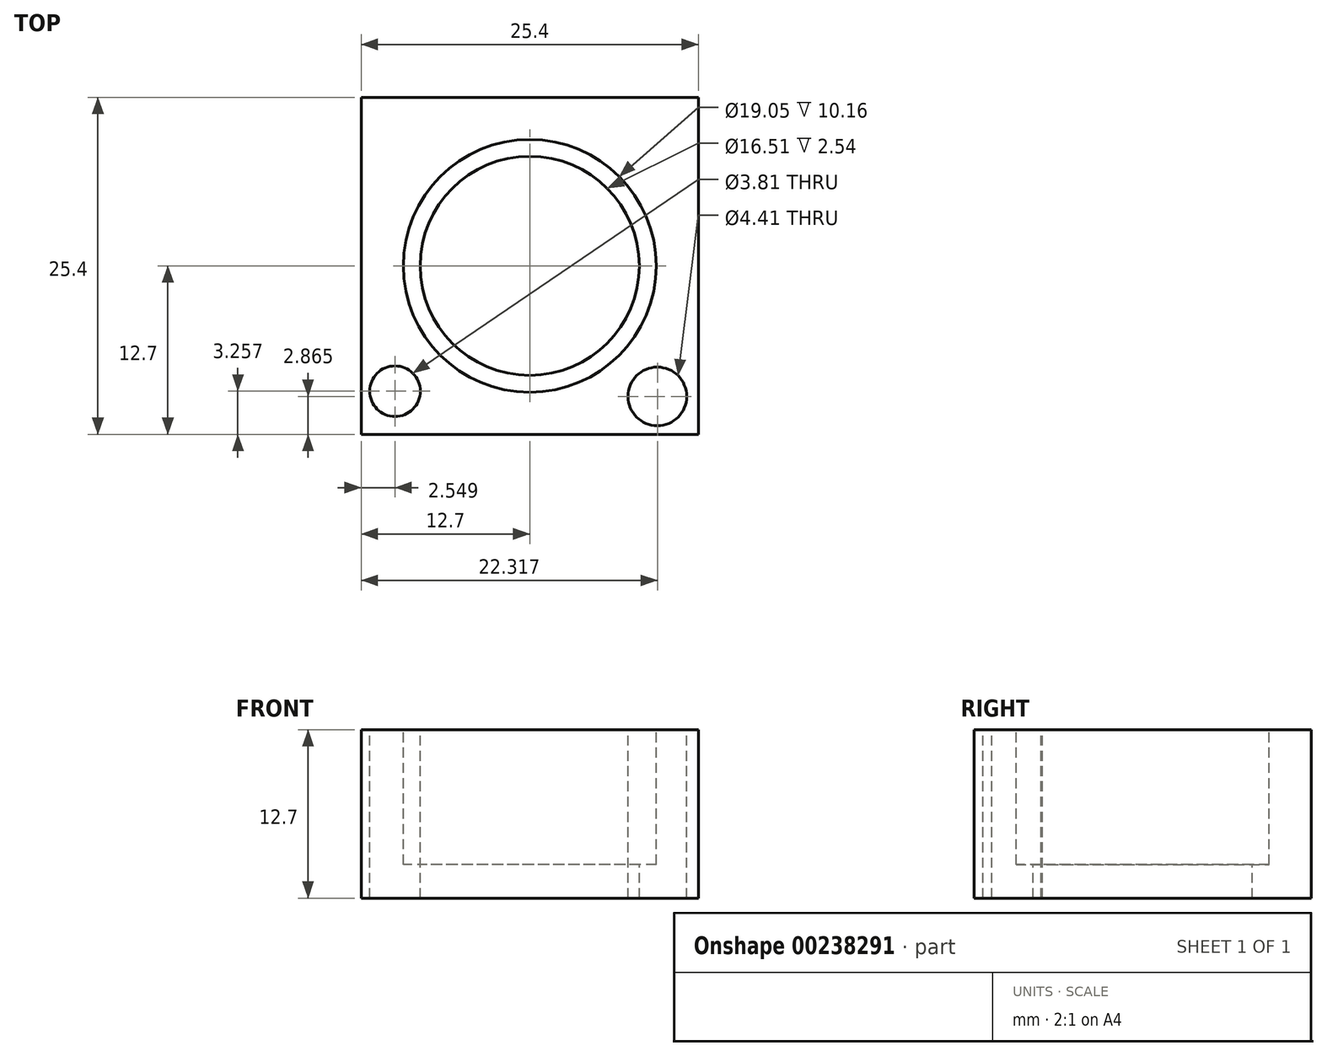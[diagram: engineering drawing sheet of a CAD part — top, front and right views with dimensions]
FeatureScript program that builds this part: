
annotation { "Feature Type Name" : "Feature", "Feature Type Description" : "" }
export const myFeature = defineFeature(function(context is Context, id is Id, definition is map)
    precondition{}
    {
        {
            var Q0;
            Q0=qCreatedBy(makeId("Top.planeOp"),FACE);
            var sketch = newSketch(context, id + "F0", { "sketchPlane" : qUnion([Q0])});
            skLineSegment(sketch, "E0.bottom", {"start": v(0, 0) * mm, "end": v(25.4, 0) * mm});
            skLineSegment(sketch, "E0.top", {"start": v(0, 25.4) * mm, "end": v(25.4, 25.4) * mm});
            skLineSegment(sketch, "E0.left", {"start": v(0, 0) * mm, "end": v(0, 25.4) * mm});
            skLineSegment(sketch, "E0.right", {"start": v(25.4, 0) * mm, "end": v(25.4, 25.4) * mm});
            skSolve(sketch);
        }
        {
            var Q0;
            Q0 = qSketchRegion(id + "F0", true);
            extrude(context, id + "F1", {"entities" : qUnion([Q0]), "depth" : 12.7 * mm});
        }
        {
            var Q0;
            Q0=makeQuery(id+"F1.opExtrude","CAP_FACE",FACE,{"disambiguationData":[OSD([sQuery(id+"F0.wireOp",EDGE,"E0.bottom"),sQuery(id+"F0.wireOp",EDGE,"E0.top"),sQuery(id+"F0.wireOp",EDGE,"E0.left"),sQuery(id+"F0.wireOp",EDGE,"E0.right")])],"isStart":false});
            var sketch = newSketch(context, id + "F2", { "sketchPlane" : qUnion([Q0])});
            skCircle(sketch, "E1", {"center": v(12.7, 12.7) * mm, "radius": 9.53 * mm});
            skPoint(sketch, "E1.centerSnap0", {"position": v(12.7, 25.4) * mm});
            skPoint(sketch, "E1.centerSnap1", {"position": v(25.4, 12.7) * mm});
            skSolve(sketch);
        }
        {
            var Q0;
            Q0 = qSketchRegion(id + "F2", true);
            extrude(context, id + "F3", {"entities" : qUnion([Q0]), "operationType" : NewBodyOperationType.REMOVE, "oppositeDirection" : true, "depth" : 10.16 * mm});
        }
        {
            var Q0;
            Q0=makeQuery(id+"F3.boolean.opBoolean","COPY",FACE,{"derivedFrom":makeQuery(id+"F3.opExtrude","CAP_FACE",FACE,{"disambiguationData":[OSD([sQuery(id+"F2.wireOp",EDGE,"E1")])],"isStart":false})});
            var sketch = newSketch(context, id + "F4", { "sketchPlane" : qUnion([Q0])});
            skCircle(sketch, "E2", {"center": v(12.7, 12.7) * mm, "radius": 8.26 * mm});
            skSolve(sketch);
        }
        {
            var Q0;
            Q0 = qSketchRegion(id + "F4", true);
            extrude(context, id + "F5", {"entities" : qUnion([Q0]), "operationType" : NewBodyOperationType.REMOVE, "endBound" : BoundingType.THROUGH_ALL, "oppositeDirection" : true, "depth" : 25.4 * mm});
        }
        {
            var Q0;
            Q0=makeQuery(id+"F1.opExtrude","CAP_FACE",FACE,{"disambiguationData":[OSD([sQuery(id+"F0.wireOp",EDGE,"E0.bottom"),sQuery(id+"F0.wireOp",EDGE,"E0.top"),sQuery(id+"F0.wireOp",EDGE,"E0.left"),sQuery(id+"F0.wireOp",EDGE,"E0.right")])],"isStart":false});
            var sketch = newSketch(context, id + "F6", { "sketchPlane" : qUnion([Q0])});
            skCircle(sketch, "E3", {"center": v(2.55, 3.26) * mm, "radius": 1.9 * mm});
            skSolve(sketch);
        }
        {
            var Q0;
            Q0 = qSketchRegion(id + "F6", true);
            extrude(context, id + "F7", {"entities" : qUnion([Q0]), "operationType" : NewBodyOperationType.REMOVE, "endBound" : BoundingType.THROUGH_ALL, "oppositeDirection" : true, "depth" : 25.4 * mm});
        }
        {
            var Q0;
            Q0=makeQuery(id+"F1.opExtrude","CAP_FACE",FACE,{"disambiguationData":[OSD([sQuery(id+"F0.wireOp",EDGE,"E0.bottom"),sQuery(id+"F0.wireOp",EDGE,"E0.top"),sQuery(id+"F0.wireOp",EDGE,"E0.left"),sQuery(id+"F0.wireOp",EDGE,"E0.right")])],"isStart":false});
            var sketch = newSketch(context, id + "F8", { "sketchPlane" : qUnion([Q0])});
            skCircle(sketch, "E4", {"center": v(22.32, 2.86) * mm, "radius": 2.2 * mm});
            skSolve(sketch);
        }
        {
            var Q0;
            Q0 = qSketchRegion(id + "F8", true);
            extrude(context, id + "F9", {"entities" : qUnion([Q0]), "operationType" : NewBodyOperationType.REMOVE, "endBound" : BoundingType.THROUGH_ALL, "oppositeDirection" : true, "depth" : 25.4 * mm});
        }
    });
